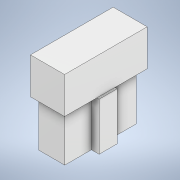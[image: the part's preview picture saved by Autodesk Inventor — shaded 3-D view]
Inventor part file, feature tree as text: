
AUTODESK INVENTOR PART (.ipt)
format: ipt  version: 2020 (Build 240168000, 168)  size: 115,712 bytes
history: native  units: mm
features: extrude x2, sketch x2, other x1
ambient origin geometry x8: Origin, YZ Plane, XZ Plane, XY Plane, X Axis, Y Axis, Z Axis, Center Point
bodies: Body1 (feature_tree)
feature tree (5):
  other  "Bryła1"
  extrude  "Wyciągnięcie proste1"  Depth=15.7mm
  extrude  "Wyciągnięcie proste2"  Depth=5.7mm
  sketch  "Szkic1"
  sketch  "Szkic2"
